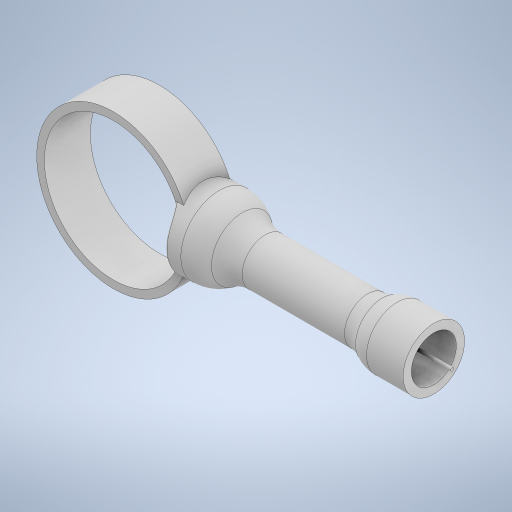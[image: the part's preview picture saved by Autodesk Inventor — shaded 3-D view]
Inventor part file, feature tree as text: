
AUTODESK INVENTOR PART (.ipt)
format: ipt  version: 2024 (Build 280153000, 153)  size: 536,064 bytes
history: native  units: mm
features: extrude x5, fillet x4, sketch x3, revolve x1, mirror x1, shell x1
ambient origin geometry x8: Origin, YZ Plane, XZ Plane, XY Plane, X Axis, Y Axis, Z Axis, Center Point
bodies: Solid1 (feature_tree)
feature tree (15):
  sketch  "Sketch1"  dims[d0=90.0mm d1=100.0mm]
  extrude  "Extrusion1"  Depth=100.0mm
  revolve  "Revolution1"  [1 undecoded]
  fillet  "Fillet1"  Radius=100.0mm
  fillet  "Fillet2"  Radius=15.0mm
  fillet  "Fillet3"  Radius=15.0mm
  mirror  "Mirror1"
  shell  "Shell1"  Thickness=15.0mm
  sketch  "Sketch2"  dims[d2=25.0mm d3=25.0mm d4=100.0mm d5=15.0mm d6=15.0mm d7=15.0mm d8=0.0mm]
  extrude  "Extrusion2"  Depth=25.0mm
  fillet  "Fillet4"  Radius=10.0mm
  extrude  "Extrusion3"  Depth=1.0mm
  extrude  "Extrusion4"  Depth=40.0mm
  extrude  "Extrusion5"  Depth=30.0mm TaperAngle=0.0deg
  sketch  "Sketch3"  dims[d9=180.0deg d10=25.0mm d11=10.0mm d12=1.0mm d13=5.0mm d14=30.0mm d15=0.0mm d16=20.0mm d17=30.0mm d18=0.0mm d19=2.0mm d20=0.0mm d21=2.0mm d22=40.0mm d23=0.0mm]
note: 1 required parameter value undecoded (feature->parameter linkage not recoverable at this tier; creation-order binding heuristic only, values carry confidence <= 0.55)
